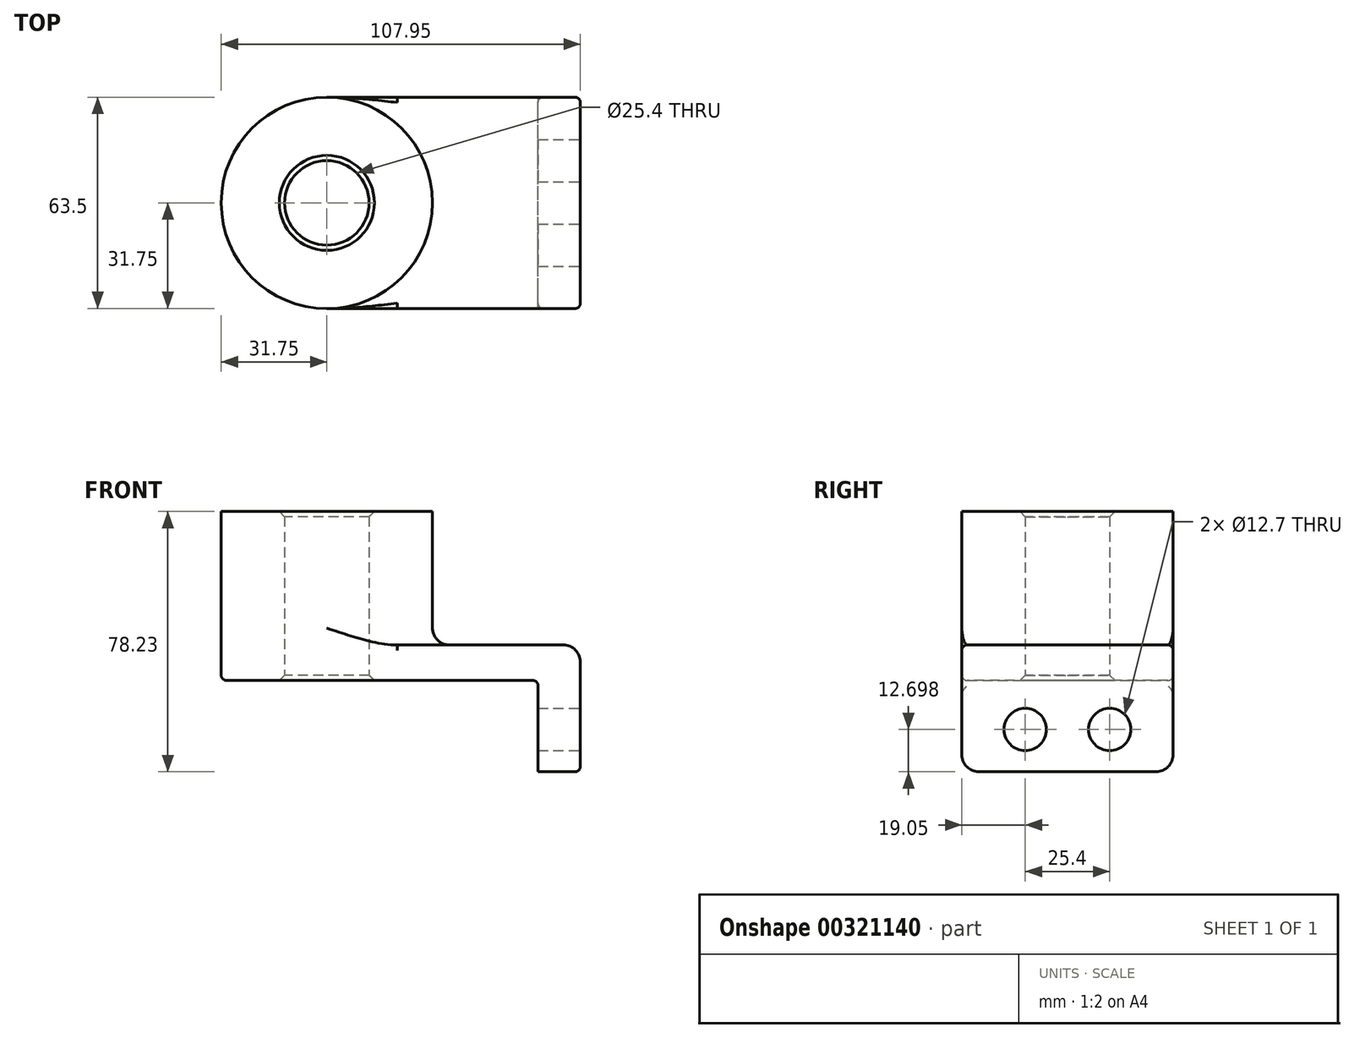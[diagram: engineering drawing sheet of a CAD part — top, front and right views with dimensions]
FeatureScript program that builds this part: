
annotation { "Feature Type Name" : "Feature", "Feature Type Description" : "" }
export const myFeature = defineFeature(function(context is Context, id is Id, definition is map)
    precondition{}
    {
        {
            var Q0;
            Q0=qCreatedBy(makeId("Top.planeOp"),FACE);
            var sketch = newSketch(context, id + "F0", { "sketchPlane" : qUnion([Q0])});
            skLineSegment(sketch, "E0.bottom", {"start": v(38.1, 31.75) * mm, "end": v(-38.1, 31.75) * mm});
            skLineSegment(sketch, "E0.top", {"start": v(38.1, -31.75) * mm, "end": v(-38.1, -31.75) * mm});
            skLineSegment(sketch, "E0.left", {"start": v(38.1, 31.75) * mm, "end": v(38.1, -31.75) * mm});
            skLineSegment(sketch, "E0.right", {"start": v(-38.1, 31.75) * mm, "end": v(-38.1, -31.75) * mm});
            skPoint(sketch, "E0.middle", {"position": v(0, 0) * mm});
            skCircle(sketch, "E1", {"center": v(-38.1, 0) * mm, "radius": 12.7 * mm});
            skCircle(sketch, "E2", {"center": v(-38.1, 0) * mm, "radius": 31.75 * mm});
            skSolve(sketch);
        }
        {
            var Q0;
            Q0 = qSketchRegion(id + "F0", true);
            extrude(context, id + "F1", {"entities" : qUnion([Q0]), "depth" : 10.67 * mm});
        }
        {
            var Q0;
            {var subQ1=sQuery(id+"F0.wireOp",EDGE,"E0.right");var subQ3=sQuery(id+"F0.wireOp",EDGE,"E1");var subQ4=makeQuery(id+"F0.imprint","INTERSECT",VERTEX,{"disambiguationData":[OD(0.0)],"derivedFrom":[subQ1,subQ3]});Q0=makeQuery(id+"F0.imprint","IMPRINT",FACE,{"disambiguationData":[TD([[makeQuery(id+"F0.imprint","IMPRINT",EDGE,{"disambiguationData":[TD([[subQ4,-1.0]])],"derivedFrom":subQ3}),-1.0]])]});}
            var Q1;
            {var subQ1=sQuery(id+"F0.wireOp",EDGE,"E0.right");var subQ3=sQuery(id+"F0.wireOp",EDGE,"E1");var subQ4=makeQuery(id+"F0.imprint","INTERSECT",VERTEX,{"disambiguationData":[OD(0.0)],"derivedFrom":[subQ1,subQ3]});Q1=makeQuery(id+"F0.imprint","IMPRINT",FACE,{"disambiguationData":[TD([[makeQuery(id+"F0.imprint","IMPRINT",EDGE,{"disambiguationData":[TD([[subQ4,1.0]])],"derivedFrom":subQ3}),-1.0]])]});}
            extrude(context, id + "F2", {"entities" : qUnion([Q0, Q1]), "operationType" : NewBodyOperationType.ADD, "depth" : 50.8 * mm});
        }
        {
            var Q0;
            Q0=makeQuery(id+"F1.opExtrude","SWEPT_FACE",FACE,{"disambiguationData":[OSD([sQuery(id+"F0.wireOp",EDGE,"E0.left")])]});
            var sketch = newSketch(context, id + "F3", { "sketchPlane" : qUnion([Q0])});
            skLineSegment(sketch, "E3.bottom", {"start": v(-31.75, 10.67) * mm, "end": v(31.75, 10.67) * mm});
            skLineSegment(sketch, "E3.top", {"start": v(-31.75, -27.43) * mm, "end": v(31.75, -27.43) * mm});
            skLineSegment(sketch, "E3.left", {"start": v(-31.75, 10.67) * mm, "end": v(-31.75, -27.43) * mm});
            skLineSegment(sketch, "E3.right", {"start": v(31.75, 10.67) * mm, "end": v(31.75, -27.43) * mm});
            skCircle(sketch, "E4", {"center": v(-12.7, -14.73) * mm, "radius": 6.35 * mm});
            skLineSegment(sketch, "E5", {"start": v(0, 0) * mm, "end": v(0, -27.43) * mm, "construction": true});
            skCircle(sketch, "E6.MirrorC", {"center": v(12.7, -14.73) * mm, "radius": 6.35 * mm});
            skSolve(sketch);
        }
        {
            var Q0;
            Q0 = qSketchRegion(id + "F3", true);
            extrude(context, id + "F4", {"entities" : qUnion([Q0]), "operationType" : NewBodyOperationType.ADD, "oppositeDirection" : true, "depth" : 12.7 * mm});
        }
        {
            var Q0;
            Q0=makeQuery(id+"F1.opExtrude","CAP_EDGE",EDGE,{"disambiguationData":[OSD([sQuery(id+"F0.wireOp",EDGE,"E0.left")])],"isStart":false});
            var Q1;
            Q1=makeQuery(id+"F4.opExtrude","SWEPT_EDGE",EDGE,{"disambiguationData":[OSD([sQuery(id+"F3.wireOp",EDGE,"E3.top"),sQuery(id+"F3.wireOp",EDGE,"E3.left")])]});
            var Q2;
            Q2=makeQuery(id+"F4.opExtrude","SWEPT_EDGE",EDGE,{"disambiguationData":[OSD([sQuery(id+"F3.wireOp",EDGE,"E3.top"),sQuery(id+"F3.wireOp",EDGE,"E3.right")])]});
            var Q3;
            {var subQ0=sQuery(id+"F0.wireOp",EDGE,"E2");Q3=makeQuery(id+"F2.boolean.opBoolean","INTERSECT",EDGE,{"derivedFrom":[makeQuery(id+"F1.opExtrude","CAP_FACE",FACE,{"disambiguationData":[OSD([sQuery(id+"F0.wireOp",EDGE,"E0.bottom"),sQuery(id+"F0.wireOp",EDGE,"E0.top"),sQuery(id+"F0.wireOp",EDGE,"E0.left"),sQuery(id+"F0.wireOp",EDGE,"E1"),subQ0])],"isStart":false}),makeQuery(id+"F2.opExtrude","SWEPT_FACE",FACE,{"disambiguationData":[OSD([subQ0])]})]});}
            fillet(context, id + "F5", {"entities" : qUnion([Q0, Q1, Q2, Q3]), "radius" : 5.08 * mm, "tangentPropagation" : true, "allowEdgeOverflow" : false});
        }
        {
            var Q0;
            Q0=makeQuery(id+"F1.opExtrude","CAP_EDGE",EDGE,{"disambiguationData":[OSD([sQuery(id+"F0.wireOp",EDGE,"E0.top")])],"isStart":false});
            var Q1;
            Q1=makeQuery(id+"F1.opExtrude","CAP_EDGE",EDGE,{"disambiguationData":[OSD([sQuery(id+"F0.wireOp",EDGE,"E0.top")])],"isStart":true});
            var Q2;
            Q2=makeQuery(id+"F4.boolean.opBoolean","INTERSECT",EDGE,{"derivedFrom":[makeQuery(id+"F1.opExtrude","CAP_FACE",FACE,{"disambiguationData":[OSD([sQuery(id+"F0.wireOp",EDGE,"E0.bottom"),sQuery(id+"F0.wireOp",EDGE,"E0.top"),sQuery(id+"F0.wireOp",EDGE,"E0.left"),sQuery(id+"F0.wireOp",EDGE,"E1"),sQuery(id+"F0.wireOp",EDGE,"E2")])],"isStart":true}),makeQuery(id+"F4.opExtrude","CAP_FACE",FACE,{"disambiguationData":[OSD([sQuery(id+"F3.wireOp",EDGE,"E3.bottom"),sQuery(id+"F3.wireOp",EDGE,"E3.top"),sQuery(id+"F3.wireOp",EDGE,"E3.left"),sQuery(id+"F3.wireOp",EDGE,"E3.right"),sQuery(id+"F3.wireOp",EDGE,"E4"),sQuery(id+"F3.wireOp",EDGE,"E6.MirrorC")])],"isStart":false})]});
            fillet(context, id + "F6", {"entities" : qUnion([Q0, Q1, Q2]), "radius" : 1.59 * mm, "tangentPropagation" : true, "allowEdgeOverflow" : false});
        }
        {
            var Q0;
            {var subQ0=sQuery(id+"F0.wireOp",EDGE,"E1");Q0=makeQuery(id+"F2.boolean.opBoolean","MERGE",FACE,{"derivedFrom":[makeQuery(id+"F1.opExtrude","SWEPT_FACE",FACE,{"disambiguationData":[OSD([subQ0])]}),makeQuery(id+"F2.opExtrude","SWEPT_FACE",FACE,{"disambiguationData":[OSD([subQ0])]})]});}
            chamfer(context, id + "F7", {"entities" : qUnion([Q0]), "width" : 1.59 * mm, "tangentPropagation" : true});
        }
    });
